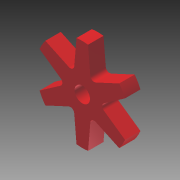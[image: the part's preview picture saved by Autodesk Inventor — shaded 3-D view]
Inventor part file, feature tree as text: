
AUTODESK INVENTOR PART (.ipt)
format: ipt  version: 2012 (Build 160160000, 160)  size: 121,856 bytes
history: native  units: in
note: dims shown in document units (in); Inventor stores cm internally (conversion verified against a paired STEP export)
features: extrude x1, fillet x1, sketch x1
ambient origin geometry x8: Origin, YZ Plane, XZ Plane, XY Plane, X Axis, Y Axis, Z Axis, Center Point
bodies: Solid1 (feature_tree)
feature tree (3):
  extrude  "Extrusion1"  Depth=0.1875in
  fillet  "Fillet1"  Radius=0.0344in
  sketch  "Sketch1"  dims[d1=0.375in d2=0.1875in d3=0.0344in d4=0.0344in d5=0.0344in d6=0.0344in d7=0.0344in d8=0.0344in d9=0.0344in d10=1.5in d11=0.5in d12=0.0in d13=0.5in d14=0.125in]
